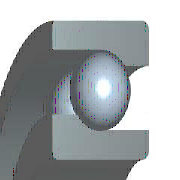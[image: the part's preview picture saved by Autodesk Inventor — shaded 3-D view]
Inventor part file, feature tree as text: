
AUTODESK INVENTOR PART (.ipt)
format: ipt  version: 2025 (Build 290162010, 162A)  size: 292,864 bytes
history: native  units: mm (DEFAULTED — no unit token found)
features: sketch x6, other x5, plane x3, fillet x2, pattern_circular x1
ambient origin geometry x8: Origin, YZ Plane, XZ Plane, XY Plane, X Axis, Y Axis, Z Axis, Center Point
bodies: Solid1 (feature_tree)
feature tree (17):
  plane  "WorkPlane1"
  plane  "Work Plane2"
  plane  "WorkPlane2"
  sketch  "Sketch1"  dims[d0=-12.0mm]
  other  "WorkPoint1"
  sketch  "Sketch2"  dims[d1=10.0mm]
  other  "WorkPoint3"
  sketch  "Sketch3"  dims[d2=8.5mm]
  other  "WorkPoint2"
  other  "WorkAxis1"
  other  "Work Axis2"
  pattern_circular  "PolarArray1"  Count=2  [1 undecoded]
  fillet  "Fillet1"  Radius=14.0mm
  fillet  "Fillet2"  Radius=12.0mm
  sketch  "Sketch4"  dims[d3=23.5mm d4=20.0mm d5=14.0mm d6=12.0mm]
  sketch  "Sketch5"  dims[d7=360.0deg]
  sketch  "Sketch6"  dims[d8=7.0mm d9=6.0mm d10=8.1mm d11=6.9mm d12=360.0deg d13=4.05mm d14=3.45mm d15=360.0deg d16=60.0mm d18=360.0deg d19=0.6mm d20=0.6mm d21=28.5mm d22=24.36mm d23=32.64mm d26=0.0mm d27=0.0mm d28=0.0mm d29=0.0mm d30=0.0mm]
note: 1 required parameter value undecoded (feature->parameter linkage not recoverable at this tier; creation-order binding heuristic only, values carry confidence <= 0.55)
